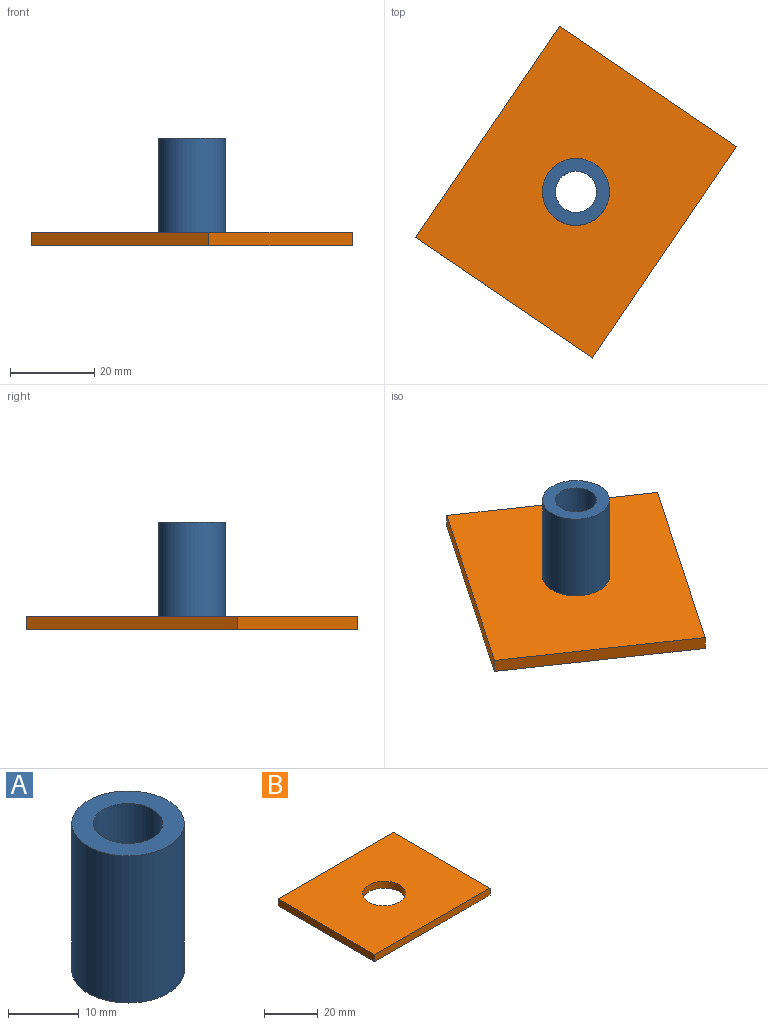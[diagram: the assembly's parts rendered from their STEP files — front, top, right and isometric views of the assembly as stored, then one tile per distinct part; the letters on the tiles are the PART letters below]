
ASSEMBLY  parts=2 mates=1
PART A: 4 faces, bbox 15.9x15.9x25.4 mm
  f0: cylinder r=4.89mm len=25.4mm, axis (0,0,-1), area 780.3mm2, adj f2,f3
  f1: cylinder r=7.94mm len=25.4mm, axis (0,0,-1), area 1266.8mm2, adj f2,f3
  f2: plane 15.88x15.88mm, normal (0,0,1), area 122.8mm2, adj f0,f1
  f3: plane 15.88x15.88mm, normal (0,0,-1), area 122.8mm2, adj f0,f1
PART B: 7 faces, bbox 60.6x50.8x3.2 mm
  f0: plane 60.58x3.18mm, normal (0,-1,0), area 192.3mm2, adj f1,f4,f5,f6
  f1: plane 50.8x3.18mm, normal (1,0,0), area 161.3mm2, adj f0,f2,f5,f6
  f2: plane 60.58x3.18mm, normal (0,1,0), area 192.3mm2, adj f1,f4,f5,f6
  f3: cylinder r=7.94mm len=15.88mm, axis (0,0,-1), area 158.3mm2, adj f5,f6
  f4: plane 50.8x3.18mm, normal (-1,0,0), area 161.3mm2, adj f0,f2,f5,f6
  f5: plane 60.58x50.8mm, normal (0,0,1), area 2879.5mm2, adj f0,f1,f2,f3,f4
  f6: plane 60.58x50.8mm, normal (0,0,-1), area 2879.5mm2, adj f0,f1,f2,f3,f4
PLACE A rot(axis=(0,0,-1),34.3deg) t=(25.83,-49.38,-10.82)mm
PLACE B rot(axis=(0,0,1),55.7deg) t=(25.83,-49.38,-10.82)mm
MATE planar A.f1 <-> B.f3  axis (0,0,-1) through (25.83,-49.38,-10.82)mm
